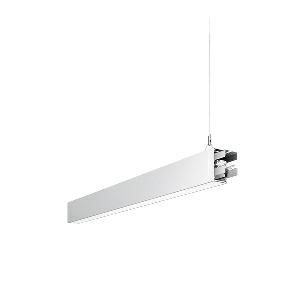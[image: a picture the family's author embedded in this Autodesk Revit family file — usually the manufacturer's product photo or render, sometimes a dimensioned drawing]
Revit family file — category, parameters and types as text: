
# Revit family: dotoo_line_-_dlp_1000_840_d_mid_00805774_c605
name_source: partatom
category: Lighting Fixtures
units: mm (PartAtom-declared; Revit-internal decimal feet)

## family parameters
Cut with Voids When Loaded = No
Host = Face
Light Source = No
Part Type = Normal
Room Calculation Point = No
Round Connector Dimension = Use Diameter
Shared = No

## types (1)
- DOTOO.line - DLP 1000/840/D MID (1 x LED, 1000 lm, 4000K)
    Apparent Load = 10 VA
    Approval mark = CE
    CIE Flux Codes = 67 91 98 100 100
    Color Rendering = 80-89
    Color Temperature = 4000K
    Control Gear = Electronic ballast
    Default Elevation = 1800 mm
    Description = DLP 1000/840/D|Suspended luminaire|light source: LED|connected load: 220-240 V, 50/60 Hz|Power consumption: approx. 9,5 W|standby: approx. 0,20|luminous flux: 1000 lm|luminous efficacy: 105 lm/W|light distribution: Direct|direct ratio: approx. 100 %|colour temperature: Cold white, ca. 4000 K|color rendering index (CRI): >= 80|chromaticity tolerance:  3 SDCM|System of protection: IP 40|technology: Continuously dimmable|luminaire body|material: Sectional aluminium|colour: White|lamp cover: Acrylic (PMMA), Clear|mains lead: 1,0 m With free stranded wires|Fastening: Steel cable 0.3 - 0.7 m|glare control: Prism aperture|luminance(L65): <= 3000 cd/m|unified glare rating(4H 8H): <=  19|special features: DALI Load 1x, TouchDIM - dimming via standard switch, Through-wired, up to 18 m on one mains connection, Flicker-free, Suitable as emergency lighting, Mechanical and electrical connection of the individual modules without tools|
    Frequency = 50 Hz
    Height = 110 mm
    Lamp = 1 x LED
    Lamp Light Flux = 1000 lm
    Lamp count = 1
    Length = 842 mm
    Luminous efficacy = 105 lm/W
    Manufacturer = Waldmann
    ModVariant = No
    Model = 00805774
    Mounting Place = Ceiling
    Mounting Type = Pendant
    Number of Poles = 1
    OnlyDefault = Yes
    Power Factor = 1
    Product Name = DOTOO.line - DLP 1000/840/D MID
    Product group = Suspended luminaire
    ProductGroupID = 9
    Protection Class = Protection class I
    Protection Degree = IP 40
    RLX_Detail_Level = 1
    RLX_Emergency_Light_Flux = 0 lm
    RLX_Emergency_Type = 0
    RLX_Emergency_Type_DB = No
    RlxData = <blob elided: 18105 chars, md5=f0177166>
    Socket = socket
    Standby Power = 0 W
    System Light Flux = 1000 lm
    System Power = 10 W
    Type Comments = Product without accessories
    Type Image = 113296000-00692546.jpg
    URL = http://relux.com
    VarID = ---
    Voltage = 230 V
    Voltage Range = 220-240 V
    Weight = 0.00 kg
    Width = 60 mm  [stored 0.19685 ft]

note: [stored X ft] marks values corroborated as IEEE doubles in the binary element streams (Revit-internal decimal feet)

## geometry (parser evidence)
native form markers: Blend x4, Sweep x12
no freeform markers — native parametric forms only
